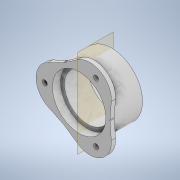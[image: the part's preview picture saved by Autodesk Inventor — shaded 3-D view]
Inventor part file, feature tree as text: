
AUTODESK INVENTOR PART (.ipt)
format: ipt  version: 2020 (Build 240168000, 168)  size: 199,680 bytes
history: native  units: in
note: dims shown in document units (in); Inventor stores cm internally (conversion verified against a paired STEP export)
features: sketch x5, projected_geometry x5, extrude x2, revolve x2, hole x1
ambient origin geometry x8: Origin, YZ Plane, XZ Plane, XY Plane, X Axis, Y Axis, Z Axis, Center Point
bodies: Solid1 (feature_tree)
feature tree (15):
  extrude  "Extrusion1"  Depth=4.0551in
  revolve  "Revolution1"  [1 undecoded]
  revolve  "Revolution2"  Angle=90.0deg
  extrude  "Extrusion2"  TaperAngle=90.0deg  [1 undecoded]
  hole  "Hole1"  [1 undecoded]
  sketch  "Sketch1"  dims[d0=2.1713in d1=4.0551in]
  sketch  "Sketch2"  dims[d2=1.5354in d3=0.0in d4=0.3937in]
  projected_geometry  "Projected Loop1"
  projected_geometry  "Projected Loop2"
  sketch  "Sketch3"  dims[d5=1.2598in d6=90.0deg]
  sketch  "Sketch4"  dims[d7=0.1969in d9=90.0deg]
  projected_geometry  "Projected Loop3"
  sketch  "Sketch5"  dims[d11=0.1969in d12=120.0deg d13=120.0deg d14=120.0deg d15=120.0deg d16=0.3937in d17=0.0in d18=0.2362in d19=1.6142in d20=1.1811in d22=360.0deg d24=0.2362in d25=0.2362in d26=0.1575in d27=0.0787in d28=90.0deg d29=0.315in d30=0.8108in]
  projected_geometry  "Project Cut Edges1"
  projected_geometry  "Project Cut Edges2"
note: 3 required parameter values undecoded (feature->parameter linkage not recoverable at this tier; creation-order binding heuristic only, values carry confidence <= 0.55)